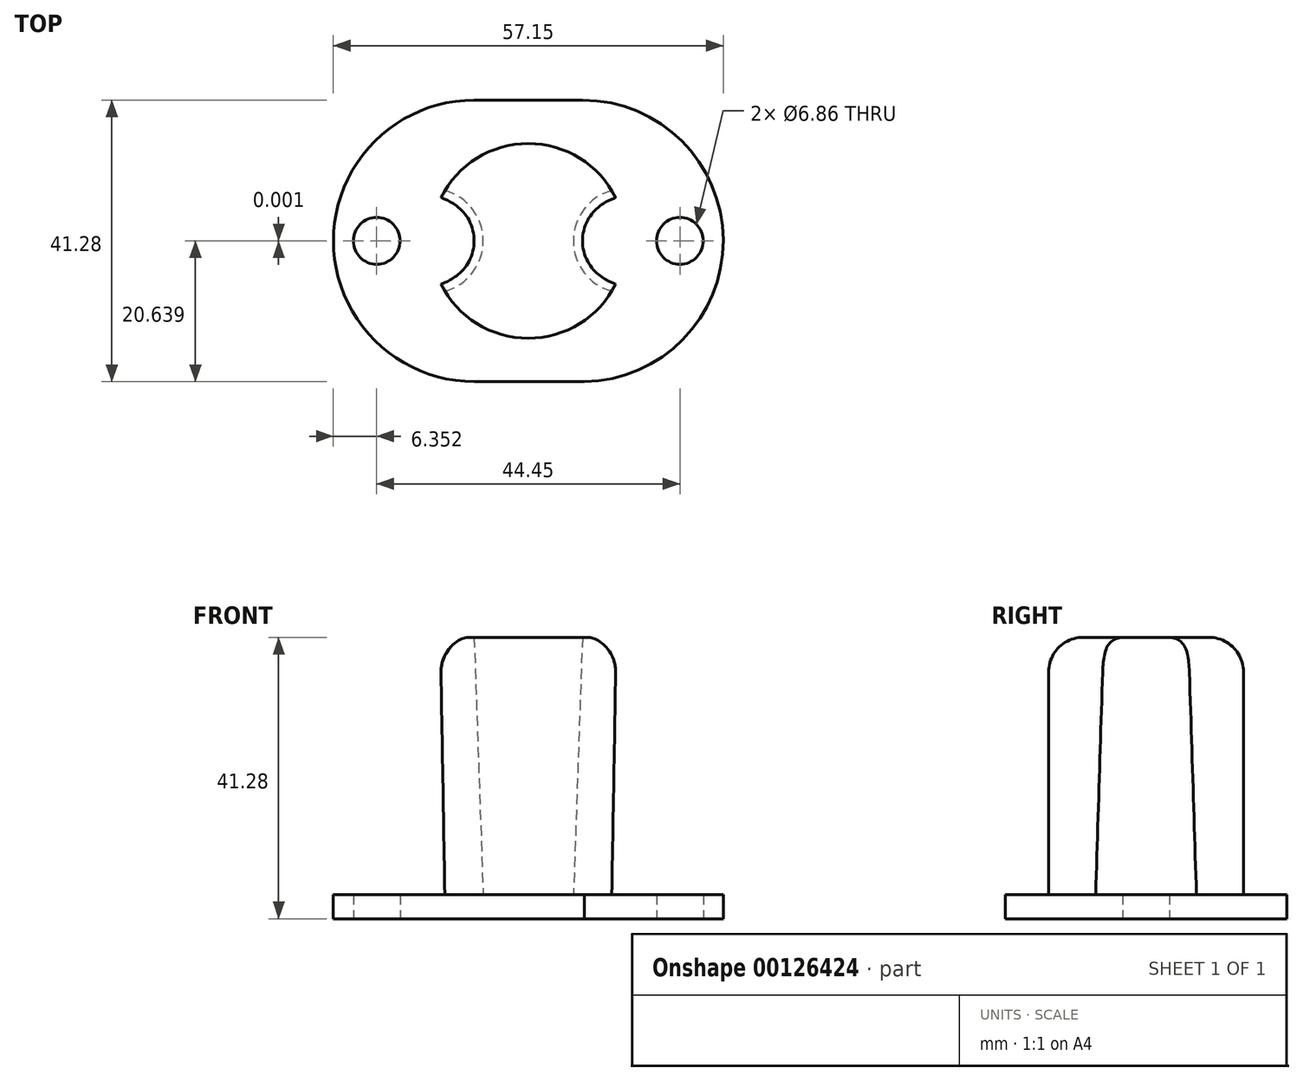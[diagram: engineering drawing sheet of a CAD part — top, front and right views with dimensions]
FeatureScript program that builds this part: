
annotation { "Feature Type Name" : "Feature", "Feature Type Description" : "" }
export const myFeature = defineFeature(function(context is Context, id is Id, definition is map)
    precondition{}
    {
        {
            var Q0;
            Q0=qCreatedBy(makeId("Top.planeOp"),FACE);
            var sketch = newSketch(context, id + "F0", { "sketchPlane" : qUnion([Q0])});
            skArc(sketch, "E0", {"start": v(-23.13, 20.64) * mm, "mid": v(-43.77, 0) * mm, "end": v(-23.13, -20.64) * mm});
            skArc(sketch, "E1", {"start": v(-7.51, -20.64) * mm, "mid": v(13.38, -0.13) * mm, "end": v(-7.26, 20.64) * mm});
            skLineSegment(sketch, "E2", {"start": v(-23.13, -20.64) * mm, "end": v(-7, -20.64) * mm});
            skLineSegment(sketch, "E3", {"start": v(-23.13, 20.64) * mm, "end": v(-7.26, 20.64) * mm});
            skPoint(sketch, "E4.startSnap0", {"position": v(-43.77, 0) * mm});
            skCircle(sketch, "E5", {"center": v(-37.42, 0) * mm, "radius": 3.43 * mm});
            skCircle(sketch, "E6", {"center": v(7.03, 0) * mm, "radius": 3.43 * mm});
            skSolve(sketch);
        }
        {
            var Q0;
            {var subQ4=sQuery(id+"F0.wireOp",EDGE,"E0");Q0=makeQuery(id+"F0.imprint","IMPRINT",FACE,{"disambiguationData":[TD([[makeQuery(id+"F0.imprint","IMPRINT",EDGE,{"derivedFrom":subQ4}),1.0]])]});}
            extrude(context, id + "F1", {"entities" : qUnion([Q0]), "depth" : 3.56 * mm});
        }
        {
            var Q0;
            Q0=makeQuery(id+"F1.opExtrude","CAP_FACE",FACE,{"disambiguationData":[OSD([sQuery(id+"F0.wireOp",EDGE,"E0"),sQuery(id+"F0.wireOp",EDGE,"E1"),sQuery(id+"F0.wireOp",EDGE,"E2"),sQuery(id+"F0.wireOp",EDGE,"E3"),sQuery(id+"F0.wireOp",EDGE,"E5"),sQuery(id+"F0.wireOp",EDGE,"E6")])],"isStart":false});
            var sketch = newSketch(context, id + "F2", { "sketchPlane" : qUnion([Q0])});
            skCircle(sketch, "E7", {"center": v(-15.2, 0) * mm, "radius": 14.29 * mm});
            skPoint(sketch, "E7.centerSnap0", {"position": v(-15.2, 20.64) * mm});
            skSolve(sketch);
        }
        {
            var Q0;
            Q0=makeQuery(id+"F2.imprint","IMPRINT",FACE,{"disambiguationData":[TD([[makeQuery(id+"F2.imprint","IMPRINT",EDGE,{"derivedFrom":sQuery(id+"F2.wireOp",EDGE,"E7")}),1.0]])]});
            var Q1;
            Q1=sQuery(id+"F2.wireOp",EDGE,"E7");
            extrude(context, id + "F3", {"entities" : qUnion([Q0]), "operationType" : NewBodyOperationType.ADD, "surfaceEntities" : qUnion([Q1]), "depth" : 37.72 * mm});
        }
        {
            var Q0;
            Q0=makeQuery(id+"F3.opExtrude","CAP_FACE",FACE,{"disambiguationData":[OSD([sQuery(id+"F2.wireOp",EDGE,"E7")])],"isStart":false});
            var sketch = newSketch(context, id + "F4", { "sketchPlane" : qUnion([Q0])});
            skCircle(sketch, "E8", {"center": v(-0.9, 0) * mm, "radius": 6.35 * mm});
            skCircle(sketch, "E9", {"center": v(-29.48, 0) * mm, "radius": 6.35 * mm});
            skSolve(sketch);
        }
        {
            var Q0;
            {var subQ0=sQuery(id+"F4.wireOp",EDGE,"E9");var subQ1=makeQuery(id+"F3.opExtrude","CAP_EDGE",EDGE,{"disambiguationData":[OSD([sQuery(id+"F2.wireOp",EDGE,"E7")])],"isStart":false});var subQ2=makeQuery(id+"F4.imprint","INTERSECT",VERTEX,{"disambiguationData":[OD(0.0)],"derivedFrom":[subQ1,subQ0]});Q0=makeQuery(id+"F4.imprint","IMPRINT",FACE,{"disambiguationData":[TD([[makeQuery(id+"F4.imprint","IMPRINT",EDGE,{"disambiguationData":[TD([[subQ2,-1.0]])],"derivedFrom":subQ0}),1.0]])]});}
            var Q1;
            {var subQ0=sQuery(id+"F4.wireOp",EDGE,"E8");var subQ1=makeQuery(id+"F3.opExtrude","CAP_EDGE",EDGE,{"disambiguationData":[OSD([sQuery(id+"F2.wireOp",EDGE,"E7")])],"isStart":false});var subQ2=makeQuery(id+"F4.imprint","INTERSECT",VERTEX,{"disambiguationData":[OD(0.0)],"derivedFrom":[subQ1,subQ0]});Q1=makeQuery(id+"F4.imprint","IMPRINT",FACE,{"disambiguationData":[TD([[makeQuery(id+"F4.imprint","IMPRINT",EDGE,{"disambiguationData":[TD([[subQ2,1.0]])],"derivedFrom":subQ0}),1.0]])]});}
            var Q2;
            Q2=sQuery(id+"F4.wireOp",EDGE,"E9");
            var Q3;
            Q3=sQuery(id+"F4.wireOp",EDGE,"E8");
            extrude(context, id + "F5", {"entities" : qUnion([Q0, Q1]), "operationType" : NewBodyOperationType.REMOVE, "surfaceEntities" : qUnion([Q2, Q3]), "oppositeDirection" : true, "depth" : 37.72 * mm, "hasDraft" : true, "draftAngle" : 2 * degree});
        }
        {
            var Q0;
            Q0=makeQuery(id+"F5.boolean.opBoolean","SPLIT",EDGE,{"disambiguationData":[OD(1.0)],"derivedFrom":makeQuery(id+"F3.opExtrude","CAP_EDGE",EDGE,{"disambiguationData":[OSD([sQuery(id+"F2.wireOp",EDGE,"E7")])],"isStart":false})});
            var Q1;
            Q1=makeQuery(id+"F5.boolean.opBoolean","SPLIT",EDGE,{"disambiguationData":[OD(0.0)],"derivedFrom":makeQuery(id+"F3.opExtrude","CAP_EDGE",EDGE,{"disambiguationData":[OSD([sQuery(id+"F2.wireOp",EDGE,"E7")])],"isStart":false})});
            fillet(context, id + "F6", {"entities" : qUnion([Q0, Q1]), "radius" : 5.08 * mm, "tangentPropagation" : true, "allowEdgeOverflow" : false});
        }
    });
